# Revit family: Accessory-Towel_Bar-KOHLER-Forte-K-11370
name_source: partatom
category: Generic Models
revit_build: Autodesk Revit 2015 (Build: 20140606_1530(x64)
units: mm (PartAtom-declared; Revit-internal decimal feet)

## types (3) — shared parameters
ADA = No
Assembly Code = C1030200
Date Modified = 11/23/2017
Default Elevation = 42"
Description = Sculpted 18 inch towel bar
Height = 3 1/2"
Length = 20 1/2"
Manufacturer = KOHLER Co.
MasterFormat 1995 = 10820
MasterFormat 2004 = 10.28.13
Material = Premium metal construction
Product Documentation Link = http://www.us.kohler.com
Product Name = Forté
Product Page URL = http://www.us.kohler.com
URL = https://www.us.kohler.com
Width = 2 1/2"

## per-type parameters (varying)
| type | Finish | Model | Type |
| CP-Polished Chrome | Kohler-Metal-CP-Polished_Chrome | K-11370-CP | 1 |
| G-Brushed Chrome | Kohler-Metal-G-Brushed_Chrome | K-11370-G | 2 |
| BN-Vibrant Brushed Nickel | Kohler-Metal-BN-Vibrant_Brushed_Nickel | K-11370-BN | 3 |

## geometry (parser evidence)
native form markers: Sweep x4
no freeform markers — native parametric forms only
